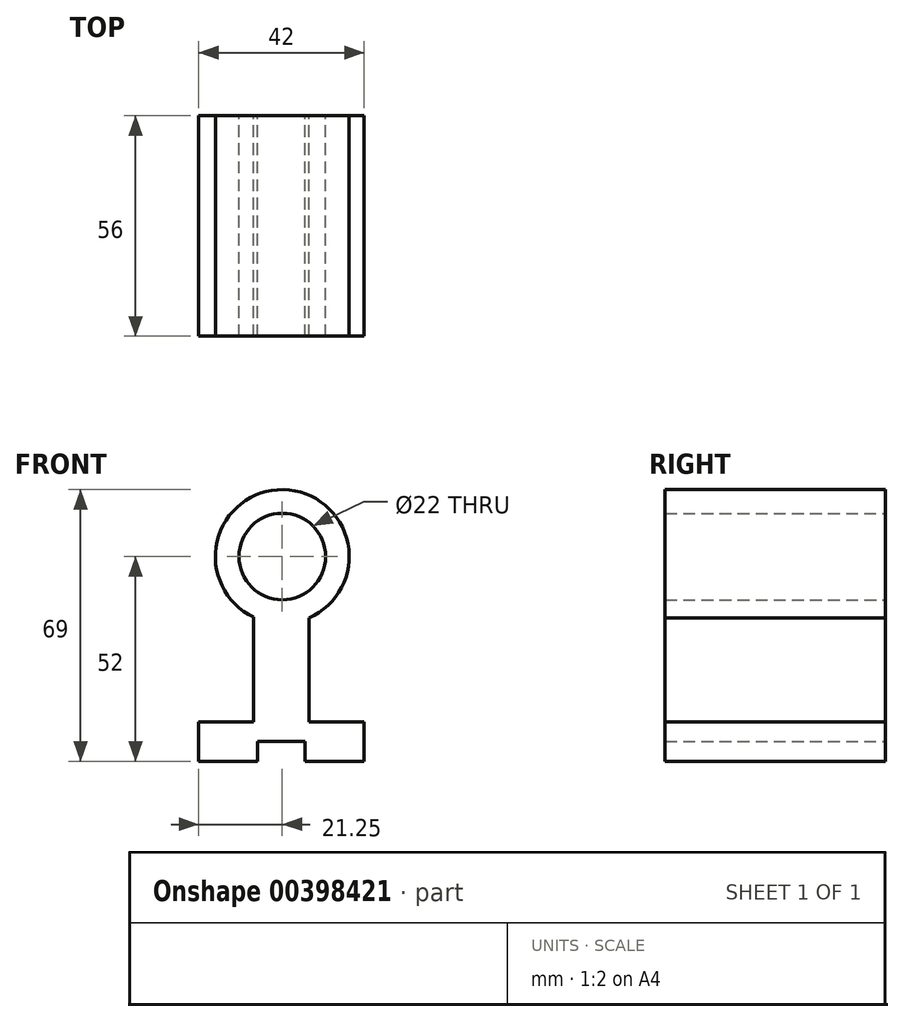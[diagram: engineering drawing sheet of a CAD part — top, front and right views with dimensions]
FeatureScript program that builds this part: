
annotation { "Feature Type Name" : "Feature", "Feature Type Description" : "" }
export const myFeature = defineFeature(function(context is Context, id is Id, definition is map)
    precondition{}
    {
        {
            var Q0;
            Q0=qCreatedBy(makeId("Front.planeOp"),FACE);
            var sketch = newSketch(context, id + "F0", { "sketchPlane" : qUnion([Q0])});
            skLineSegment(sketch, "E0", {"start": v(-6.25, 0) * mm, "end": v(-6.25, 5) * mm});
            skLineSegment(sketch, "E1", {"start": v(-6.25, 5) * mm, "end": v(5.75, 5) * mm});
            skLineSegment(sketch, "E2", {"start": v(5.75, 5) * mm, "end": v(5.75, 0) * mm});
            skLineSegment(sketch, "E3", {"start": v(5.75, 0) * mm, "end": v(20.75, 0) * mm});
            skLineSegment(sketch, "E4", {"start": v(-6.25, 0) * mm, "end": v(-21.25, 0) * mm});
            skLineSegment(sketch, "E5", {"start": v(-21.25, 0) * mm, "end": v(-21.25, 10) * mm});
            skLineSegment(sketch, "E6", {"start": v(20.75, 0) * mm, "end": v(20.75, 10) * mm});
            skLineSegment(sketch, "E7", {"start": v(20.75, 10) * mm, "end": v(6.75, 10) * mm});
            skLineSegment(sketch, "E8", {"start": v(-21.25, 10) * mm, "end": v(-7.25, 10) * mm});
            skLineSegment(sketch, "E9", {"start": v(0, 0) * mm, "end": v(0, 52) * mm});
            skCircle(sketch, "E10", {"center": v(0, 52) * mm, "radius": 11 * mm});
            skCircle(sketch, "E11", {"center": v(0, 52) * mm, "radius": 17 * mm});
            skLineSegment(sketch, "E12", {"start": v(-7.25, 10) * mm, "end": v(-7.25, 36.62) * mm});
            skLineSegment(sketch, "E13", {"start": v(6.75, 10) * mm, "end": v(6.75, 36.4) * mm});
            skSolve(sketch);
        }
        {
            var Q0;
            {var subQ0=sQuery(id+"F0.wireOp",EDGE,"E2");Q0=makeQuery(id+"F0.imprint","IMPRINT",FACE,{"disambiguationData":[TD([[makeQuery(id+"F0.imprint","IMPRINT",EDGE,{"derivedFrom":subQ0}),1.0]])]});}
            var Q1;
            {var subQ1=sQuery(id+"F0.wireOp",EDGE,"E0");Q1=makeQuery(id+"F0.imprint","IMPRINT",FACE,{"disambiguationData":[TD([[makeQuery(id+"F0.imprint","IMPRINT",EDGE,{"derivedFrom":subQ1}),1.0]])]});}
            var Q2;
            Q2=makeQuery(id+"F0.imprint","IMPRINT",FACE,{"disambiguationData":[TD([[makeQuery(id+"F0.imprint","IMPRINT",EDGE,{"derivedFrom":sQuery(id+"F0.wireOp",EDGE,"E10")}),-1.0]])]});
            extrude(context, id + "F1", {"entities" : qUnion([Q0, Q1, Q2]), "depth" : 56 * mm});
        }
    });
